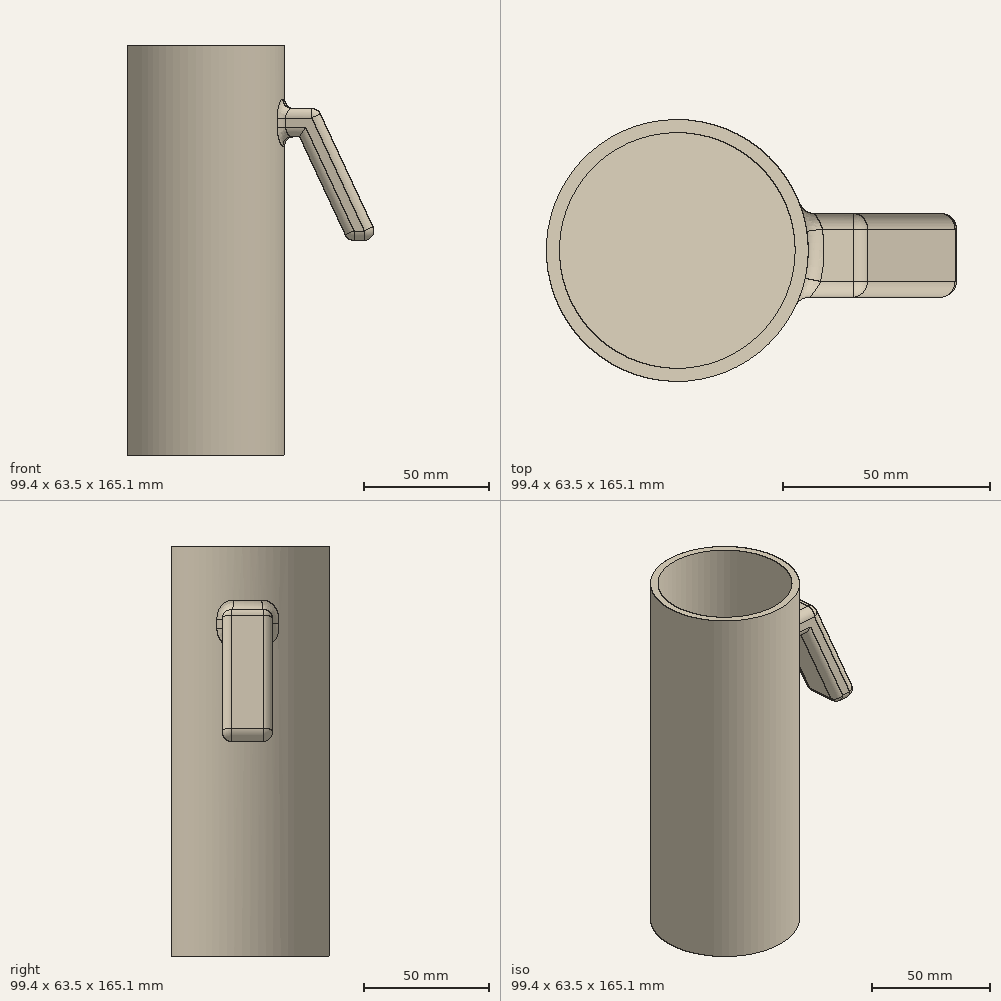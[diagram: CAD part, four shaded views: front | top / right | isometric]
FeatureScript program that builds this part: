
annotation { "Feature Type Name" : "Feature", "Feature Type Description" : "" }
export const myFeature = defineFeature(function(context is Context, id is Id, definition is map)
    precondition{}
    {
        {
            var Q0;
            Q0=qCreatedBy(makeId("Top.planeOp"),FACE);
            var sketch = newSketch(context, id + "F0", { "sketchPlane" : qUnion([Q0])});
            skCircle(sketch, "E0", {"center": v(0.6, 11.34) * mm, "radius": 31.75 * mm});
            skCircle(sketch, "E1", {"center": v(0.6, 11.34) * mm, "radius": 28.58 * mm});
            skSolve(sketch);
        }
        {
            var Q0;
            Q0=makeQuery(id+"F0.imprint","IMPRINT",FACE,{"disambiguationData":[TD([[makeQuery(id+"F0.imprint","IMPRINT",EDGE,{"derivedFrom":sQuery(id+"F0.wireOp",EDGE,"E1")}),1.0]])]});
            var Q1;
            Q1=makeQuery(id+"F0.imprint","IMPRINT",FACE,{"disambiguationData":[TD([[makeQuery(id+"F0.imprint","IMPRINT",EDGE,{"derivedFrom":sQuery(id+"F0.wireOp",EDGE,"E0")}),1.0]])]});
            extrude(context, id + "F1", {"entities" : qUnion([Q0, Q1]), "oppositeDirection" : true, "depth" : 165.1 * mm});
        }
        {
            var Q0;
            Q0=qCreatedBy(makeId("Front.planeOp"),FACE);
            var sketch = newSketch(context, id + "F2", { "sketchPlane" : qUnion([Q0])});
            skLineSegment(sketch, "E2", {"start": v(29.82, -25.4) * mm, "end": v(45.7, -25.4) * mm});
            skLineSegment(sketch, "E3", {"start": v(45.7, -25.4) * mm, "end": v(70.46, -78.5) * mm});
            skLineSegment(sketch, "E4", {"start": v(70.46, -78.5) * mm, "end": v(57.85, -78.5) * mm});
            skLineSegment(sketch, "E5", {"start": v(57.85, -78.5) * mm, "end": v(38.41, -36.83) * mm});
            skLineSegment(sketch, "E6", {"start": v(38.41, -36.83) * mm, "end": v(29.82, -36.83) * mm});
            skLineSegment(sketch, "E7", {"start": v(29.82, -36.83) * mm, "end": v(29.82, -25.4) * mm});
            skLineSegment(sketch, "E8.0", {"start": v(-31.14, 0) * mm, "end": v(32.36, 0) * mm});
            skSolve(sketch);
        }
        {
            var Q0;
            Q0=makeQuery(id+"F2.imprint","IMPRINT",FACE,{"disambiguationData":[TD([[makeQuery(id+"F2.imprint","IMPRINT",EDGE,{"derivedFrom":sQuery(id+"F2.wireOp",EDGE,"E2")}),-1.0]])]});
            extrude(context, id + "F3", {"entities" : qUnion([Q0]), "operationType" : NewBodyOperationType.ADD, "oppositeDirection" : true, "depth" : 20.32 * mm});
        }
        {
            var Q0;
            Q0=makeQuery(id+"F3.boolean.opBoolean","INTERSECT",EDGE,{"derivedFrom":[makeQuery(id+"F1.opExtrude","SWEPT_FACE",FACE,{"disambiguationData":[OSD([sQuery(id+"F0.wireOp",EDGE,"E0")])]}),makeQuery(id+"F3.opExtrude","SWEPT_FACE",FACE,{"disambiguationData":[OSD([sQuery(id+"F2.wireOp",EDGE,"E2")])]})]});
            var Q1;
            Q1=makeQuery(id+"F3.boolean.opBoolean","INTERSECT",EDGE,{"derivedFrom":[makeQuery(id+"F1.opExtrude","SWEPT_FACE",FACE,{"disambiguationData":[OSD([sQuery(id+"F0.wireOp",EDGE,"E0")])]}),makeQuery(id+"F3.opExtrude","CAP_FACE",FACE,{"disambiguationData":[OSD([sQuery(id+"F2.wireOp",EDGE,"E2"),sQuery(id+"F2.wireOp",EDGE,"E3"),sQuery(id+"F2.wireOp",EDGE,"E4"),sQuery(id+"F2.wireOp",EDGE,"E5"),sQuery(id+"F2.wireOp",EDGE,"E6"),sQuery(id+"F2.wireOp",EDGE,"E7")])],"isStart":true})]});
            var Q2;
            Q2=makeQuery(id+"F3.boolean.opBoolean","INTERSECT",EDGE,{"derivedFrom":[makeQuery(id+"F1.opExtrude","SWEPT_FACE",FACE,{"disambiguationData":[OSD([sQuery(id+"F0.wireOp",EDGE,"E0")])]}),makeQuery(id+"F3.opExtrude","SWEPT_FACE",FACE,{"disambiguationData":[OSD([sQuery(id+"F2.wireOp",EDGE,"E6")])]})]});
            var Q3;
            Q3=makeQuery(id+"F3.opExtrude","CAP_EDGE",EDGE,{"disambiguationData":[OSD([sQuery(id+"F2.wireOp",EDGE,"E2")])],"isStart":true});
            var Q4;
            Q4=makeQuery(id+"F3.opExtrude","CAP_EDGE",EDGE,{"disambiguationData":[OSD([sQuery(id+"F2.wireOp",EDGE,"E2")])],"isStart":false});
            var Q5;
            Q5=makeQuery(id+"F3.opExtrude","CAP_EDGE",EDGE,{"disambiguationData":[OSD([sQuery(id+"F2.wireOp",EDGE,"E6")])],"isStart":true});
            var Q6;
            Q6=makeQuery(id+"F3.opExtrude","CAP_EDGE",EDGE,{"disambiguationData":[OSD([sQuery(id+"F2.wireOp",EDGE,"E6")])],"isStart":false});
            fillet(context, id + "F4", {"entities" : qUnion([Q0, Q1, Q2, Q3, Q4, Q5, Q6]), "radius" : 3.8 * mm, "tangentPropagation" : true, "allowEdgeOverflow" : false});
        }
        {
            var Q0;
            Q0=makeQuery(id+"F4.opFillet","BLEND_EDGE",EDGE,{"blendedFrom":[makeQuery(id+"F3.opExtrude","CAP_EDGE",EDGE,{"disambiguationData":[OSD([sQuery(id+"F2.wireOp",EDGE,"E2")])],"isStart":true}),makeQuery(id+"F3.opExtrude","SWEPT_FACE",FACE,{"disambiguationData":[OSD([sQuery(id+"F2.wireOp",EDGE,"E3")])]})],"blendedInto":[makeQuery(id+"F3.opExtrude","SWEPT_FACE",FACE,{"disambiguationData":[OSD([sQuery(id+"F2.wireOp",EDGE,"E3")])]})]});
            var Q1;
            Q1=makeQuery(id+"F3.opExtrude","SWEPT_FACE",FACE,{"disambiguationData":[OSD([sQuery(id+"F2.wireOp",EDGE,"E4")])]});
            var Q2;
            Q2=makeQuery(id+"F3.opExtrude","CAP_EDGE",EDGE,{"disambiguationData":[OSD([sQuery(id+"F2.wireOp",EDGE,"E5")])],"isStart":false});
            var Q3;
            Q3=makeQuery(id+"F3.opExtrude","CAP_EDGE",EDGE,{"disambiguationData":[OSD([sQuery(id+"F2.wireOp",EDGE,"E5")])],"isStart":true});
            fillet(context, id + "F5", {"entities" : qUnion([Q0, Q1, Q2, Q3]), "radius" : 3.8 * mm, "tangentPropagation" : true, "allowEdgeOverflow" : false});
        }
        {
            var Q0;
            Q0=makeQuery(id+"F0.imprint","IMPRINT",FACE,{"disambiguationData":[TD([[makeQuery(id+"F0.imprint","IMPRINT",EDGE,{"derivedFrom":sQuery(id+"F0.wireOp",EDGE,"E1")}),1.0]])]});
            extrude(context, id + "F6", {"entities" : qUnion([Q0]), "operationType" : NewBodyOperationType.REMOVE, "oppositeDirection" : true, "depth" : 161.92 * mm});
        }
    });
